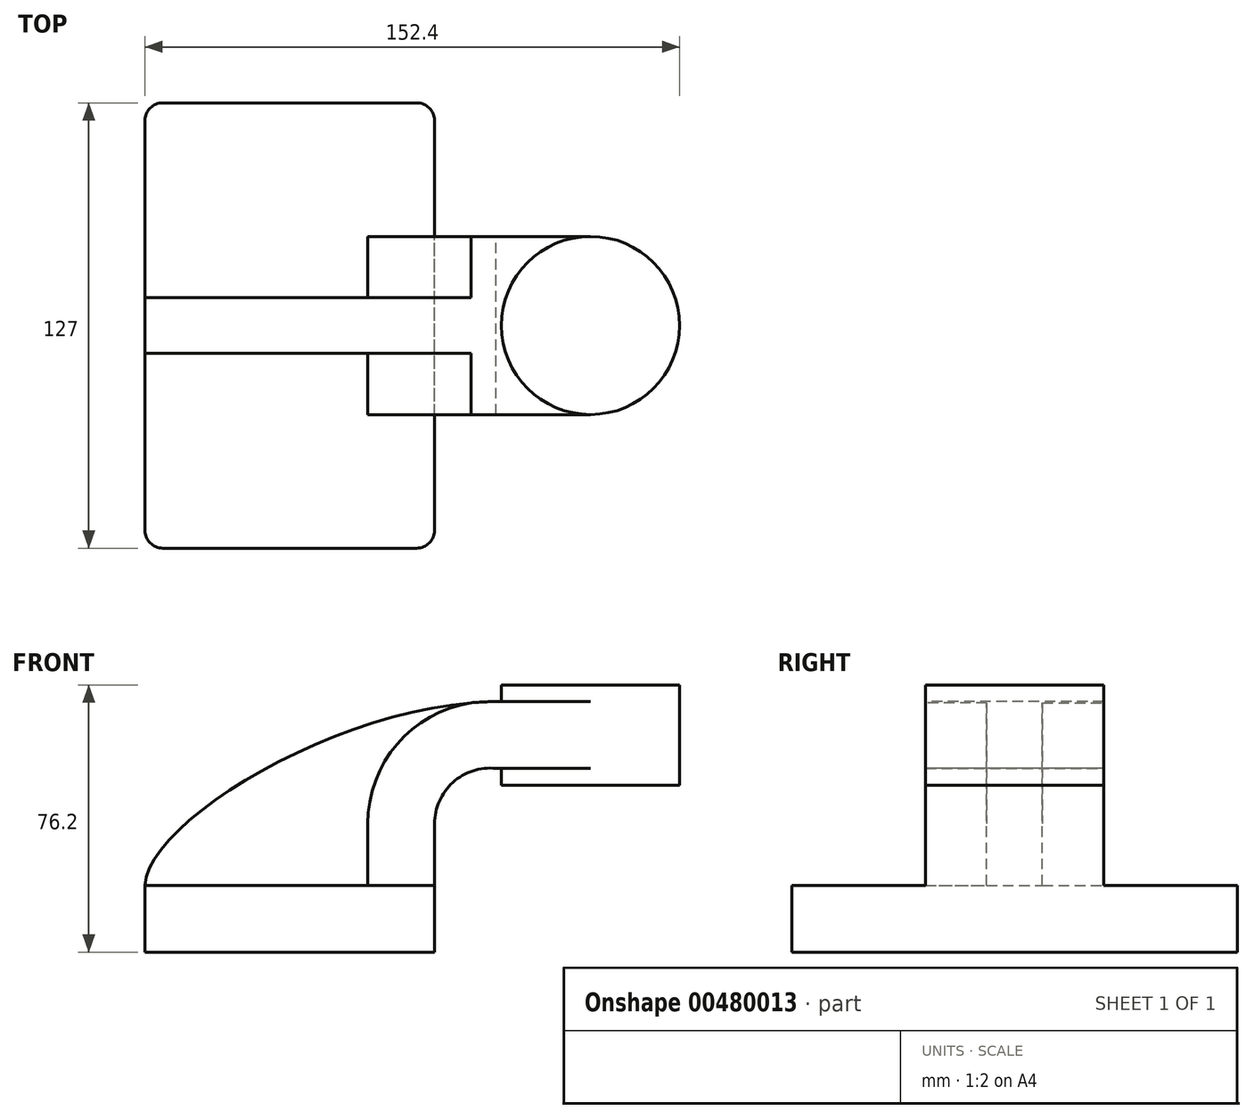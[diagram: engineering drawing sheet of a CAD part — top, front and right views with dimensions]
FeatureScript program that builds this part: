
annotation { "Feature Type Name" : "Feature", "Feature Type Description" : "" }
export const myFeature = defineFeature(function(context is Context, id is Id, definition is map)
    precondition{}
    {
        {
            var Q0;
            Q0=qCreatedBy(makeId("Front.planeOp"),FACE);
            var sketch = newSketch(context, id + "F0", { "sketchPlane" : qUnion([Q0])});
            skLineSegment(sketch, "E0.bottom", {"start": v(-32.74, 6.92) * mm, "end": v(49.81, 6.92) * mm});
            skLineSegment(sketch, "E0.top", {"start": v(-32.74, -12.13) * mm, "end": v(49.81, -12.13) * mm});
            skLineSegment(sketch, "E0.left", {"start": v(-32.74, 6.92) * mm, "end": v(-32.74, -12.13) * mm});
            skLineSegment(sketch, "E0.right", {"start": v(49.81, 6.92) * mm, "end": v(49.81, -12.13) * mm});
            skLineSegment(sketch, "E1.bottom", {"start": v(119.66, 35.5) * mm, "end": v(68.86, 35.5) * mm});
            skLineSegment(sketch, "E1.top", {"start": v(119.66, 64.07) * mm, "end": v(68.86, 64.07) * mm});
            skLineSegment(sketch, "E1.left", {"start": v(119.66, 35.5) * mm, "end": v(119.66, 64.07) * mm});
            skLineSegment(sketch, "E1.right", {"start": v(68.86, 35.5) * mm, "end": v(68.86, 64.07) * mm});
            skPoint(sketch, "E1.middle", {"position": v(94.26, 49.78) * mm});
            skLineSegment(sketch, "E2", {"start": v(49.81, 6.92) * mm, "end": v(49.81, 24.47) * mm});
            skArc(sketch, "E3", {"start": v(49.81, 24.47) * mm, "mid": v(55.04, 36.24) * mm, "end": v(67.27, 40.27) * mm});
            skLineSegment(sketch, "E4", {"start": v(67.27, 40.27) * mm, "end": v(94.26, 40.27) * mm});
            skLineSegment(sketch, "E5.0", {"start": v(68.03, 59.32) * mm, "end": v(94.26, 59.32) * mm});
            skArc(sketch, "E5.1", {"start": v(30.76, 24.47) * mm, "mid": v(41.84, 49.98) * mm, "end": v(68.03, 59.32) * mm});
            skLineSegment(sketch, "E5.2", {"start": v(30.76, 6.92) * mm, "end": v(30.76, 24.47) * mm});
            skLineSegment(sketch, "E6", {"start": v(94.26, 64.07) * mm, "end": v(94.26, 35.5) * mm});
            skFitSpline(sketch, "E7", {"points": [v(-32.74, 6.92) * mm, v(68.03, 59.32) * mm], "startDerivative": vector(2.23, 55.95) * mm, "endDerivative": vector(131.33, 0.19) * mm});
            skSolve(sketch);
        }
        {
            var Q0;
            Q0=makeQuery(id+"F0.imprint","IMPRINT",FACE,{"disambiguationData":[TD([[makeQuery(id+"F0.imprint","IMPRINT",EDGE,{"derivedFrom":sQuery(id+"F0.wireOp",EDGE,"E0.top")}),1.0]])]});
            extrude(context, id + "F1", {"entities" : qUnion([Q0]), "endBound" : BoundingType.SYMMETRIC, "depth" : 127 * mm});
        }
        {
            var Q0;
            {var subQ0=sQuery(id+"F0.wireOp",EDGE,"E5.2");Q0=makeQuery(id+"F0.imprint","IMPRINT",FACE,{"disambiguationData":[TD([[makeQuery(id+"F0.imprint","IMPRINT",EDGE,{"derivedFrom":subQ0}),1.0]])]});}
            extrude(context, id + "F2", {"entities" : qUnion([Q0]), "operationType" : NewBodyOperationType.ADD, "endBound" : BoundingType.SYMMETRIC, "depth" : 15.88 * mm});
        }
        {
            var Q0;
            {var subQ1=sQuery(id+"F0.wireOp",EDGE,"E2");Q0=makeQuery(id+"F0.imprint","IMPRINT",FACE,{"disambiguationData":[TD([[makeQuery(id+"F0.imprint","IMPRINT",EDGE,{"derivedFrom":subQ1}),1.0]])]});}
            var Q1;
            {var subQ1=sQuery(id+"F0.wireOp",EDGE,"E4");Q1=makeQuery(id+"F0.imprint","IMPRINT",FACE,{"disambiguationData":[TD([[makeQuery(id+"F0.imprint","IMPRINT",EDGE,{"derivedFrom":subQ1}),1.0]])]});}
            extrude(context, id + "F3", {"entities" : qUnion([Q0, Q1]), "operationType" : NewBodyOperationType.ADD, "endBound" : BoundingType.SYMMETRIC, "depth" : 50.8 * mm});
        }
        {
            var Q0;
            {var subQ0=sQuery(id+"F0.wireOp",EDGE,"E1.left");Q0=makeQuery(id+"F0.imprint","IMPRINT",FACE,{"disambiguationData":[TD([[makeQuery(id+"F0.imprint","IMPRINT",EDGE,{"derivedFrom":subQ0}),1.0]])]});}
            var Q1;
            Q1=sQuery(id+"F0.wireOp",EDGE,"E6");
            revolve(context, id + "F4", {"operationType" : NewBodyOperationType.ADD, "entities" : qUnion([Q0]), "axis" : qUnion([Q1]), "revolveType" : RevolveType.FULL});
        }
        {
            var Q0;
            Q0=makeQuery(id+"F1.opExtrude","CAP_EDGE",EDGE,{"disambiguationData":[OSD([sQuery(id+"F0.wireOp",EDGE,"E0.left")])],"isStart":false});
            var Q1;
            Q1=makeQuery(id+"F1.opExtrude","CAP_EDGE",EDGE,{"disambiguationData":[OSD([sQuery(id+"F0.wireOp",EDGE,"E0.right")])],"isStart":false});
            var Q2;
            Q2=makeQuery(id+"F1.opExtrude","CAP_EDGE",EDGE,{"disambiguationData":[OSD([sQuery(id+"F0.wireOp",EDGE,"E0.left")])],"isStart":true});
            var Q3;
            Q3=makeQuery(id+"F1.opExtrude","CAP_EDGE",EDGE,{"disambiguationData":[OSD([sQuery(id+"F0.wireOp",EDGE,"E0.right")])],"isStart":true});
            fillet(context, id + "F5", {"entities" : qUnion([Q0, Q1, Q2, Q3]), "radius" : 5.08 * mm, "tangentPropagation" : true, "allowEdgeOverflow" : false});
        }
    });
